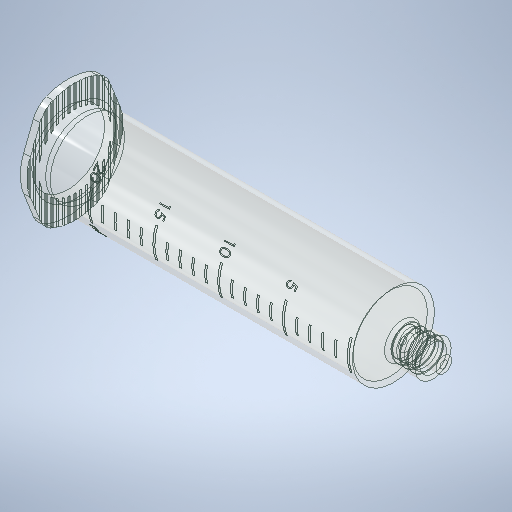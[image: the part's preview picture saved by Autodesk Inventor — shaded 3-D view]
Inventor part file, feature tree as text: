
AUTODESK INVENTOR PART (.ipt)
format: ipt  version: 2025.2 (Build 292293000, 293)  size: 1,578,496 bytes
history: native  units: in
note: dims shown in document units (in); Inventor stores cm internally (conversion verified against a paired STEP export)
features: thread x1
ambient origin geometry x8: Origin, YZ Plane, XZ Plane, XY Plane, X Axis, Y Axis, Z Axis, Center Point
bodies: Solid1 (feature_tree)
feature tree (1):
  thread  "Thread1"  [1 undecoded]
note: 1 required parameter value undecoded (feature->parameter linkage not recoverable at this tier; creation-order binding heuristic only, values carry confidence <= 0.55)
